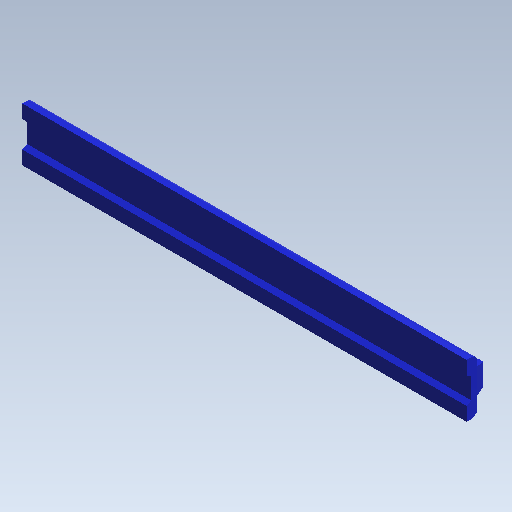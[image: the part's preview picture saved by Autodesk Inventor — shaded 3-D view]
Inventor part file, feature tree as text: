
AUTODESK INVENTOR PART (.ipt)
format: ipt  version: 2020.3 (Build 243373000, 373)  size: 198,144 bytes
history: native  units: mm (DEFAULTED — no unit token found)
features: extrude x2, sketch x2, pattern_linear x1
ambient origin geometry x8: Origin, YZ Plane, XZ Plane, XY Plane, X Axis, Y Axis, Z Axis, Center Point
bodies: Solid1 (feature_tree)
feature tree (5):
  extrude  "Extrusion1"  Depth=5.0mm TaperAngle=0.0deg
  extrude  "Extrusion2"  [1 undecoded]
  pattern_linear  "Rectangular Pattern1"  [2 undecoded]
  sketch  "Sketch_1"  dims[d0=83.0mm d1=0.0mm d2=5.0mm d3=0.0mm]
  sketch  "Sketch_5"  dims[d4=6410.0mm d6=3.14159mm d7=10.0mm d9=0.0mm]
note: 3 required parameter values undecoded (feature->parameter linkage not recoverable at this tier; creation-order binding heuristic only, values carry confidence <= 0.55)
